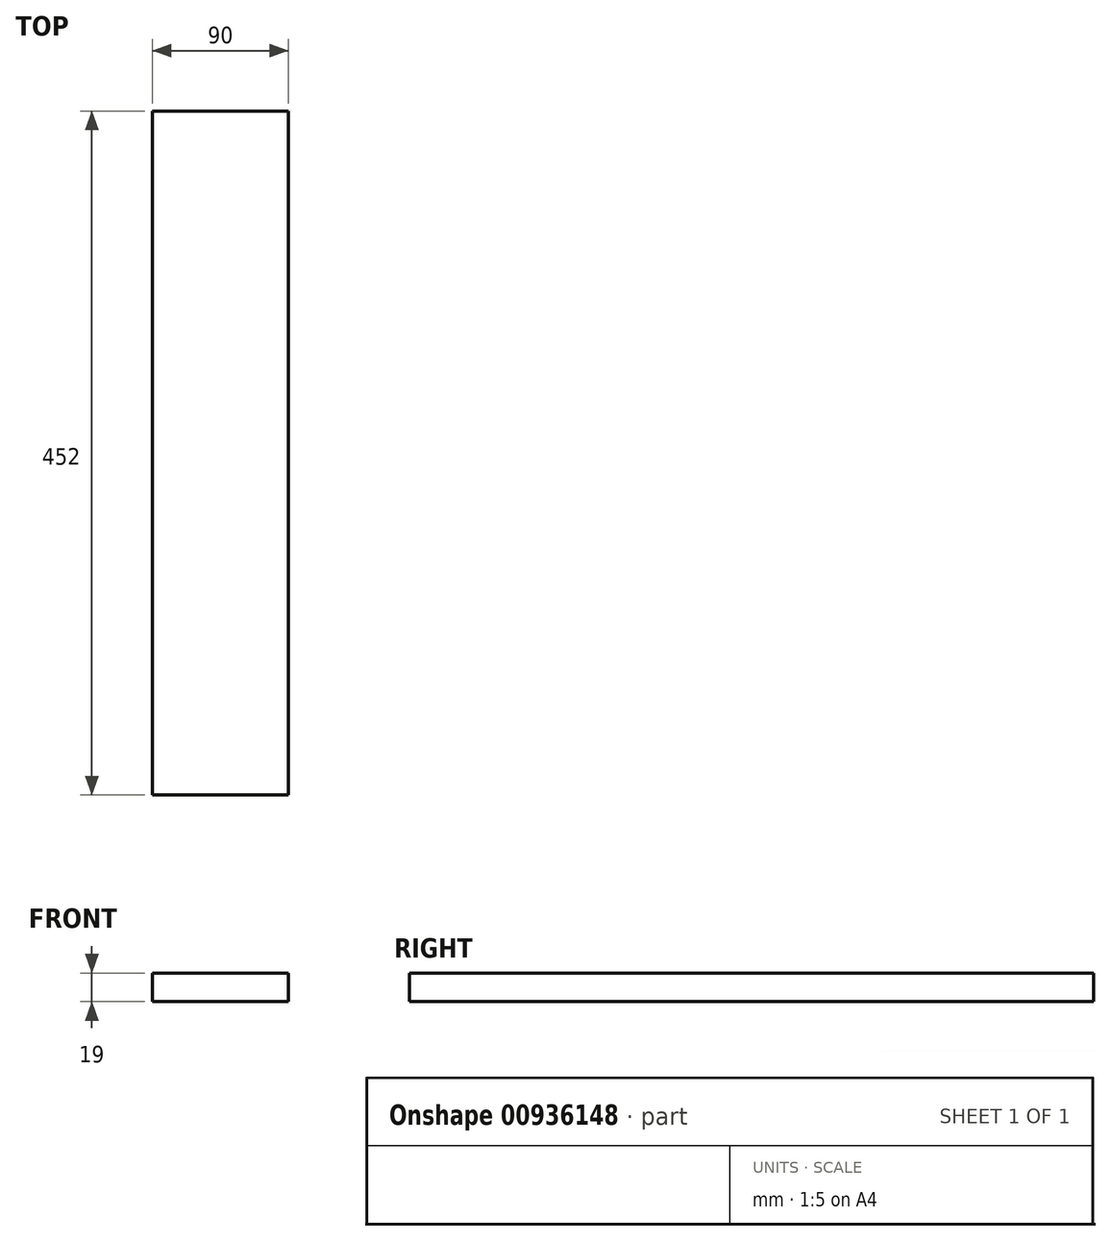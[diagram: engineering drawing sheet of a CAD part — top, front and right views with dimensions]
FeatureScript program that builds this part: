
annotation { "Feature Type Name" : "Feature", "Feature Type Description" : "" }
export const myFeature = defineFeature(function(context is Context, id is Id, definition is map)
    precondition{}
    {
        {
            var Q0;
            Q0=qCreatedBy(makeId("Front.planeOp"),FACE);
            var sketch = newSketch(context, id + "F0", { "sketchPlane" : qUnion([Q0])});
            skLineSegment(sketch, "E0.bottom", {"start": v(0, 0) * mm, "end": v(90, 0) * mm});
            skLineSegment(sketch, "E0.top", {"start": v(0, 19) * mm, "end": v(90, 19) * mm});
            skLineSegment(sketch, "E0.left", {"start": v(0, 0) * mm, "end": v(0, 19) * mm});
            skLineSegment(sketch, "E0.right", {"start": v(90, 0) * mm, "end": v(90, 19) * mm});
            skSolve(sketch);
        }
        {
            var Q0;
            Q0=makeQuery(id+"F0.imprint","IMPRINT",FACE,{"disambiguationData":[TD([[makeQuery(id+"F0.imprint","IMPRINT",EDGE,{"derivedFrom":sQuery(id+"F0.wireOp",EDGE,"E0.bottom")}),1.0]])]});
            extrude(context, id + "F1", {"entities" : qUnion([Q0]), "depth" : 452 * mm, "offsetDistance" : 25 * mm});
        }
    });
